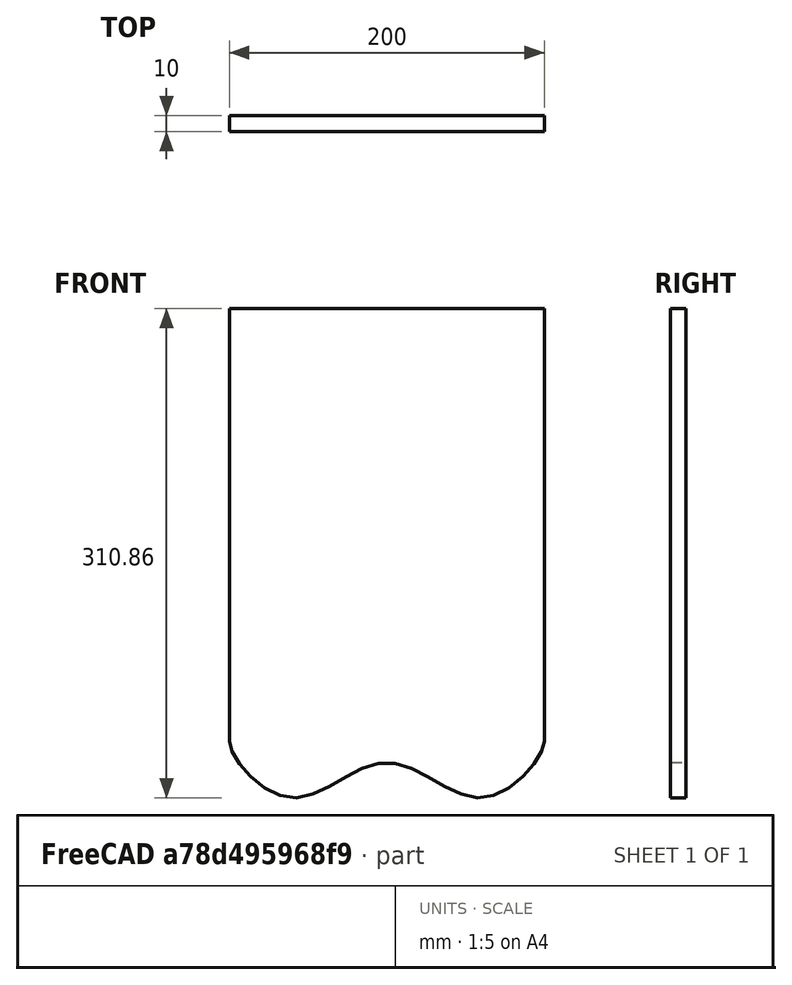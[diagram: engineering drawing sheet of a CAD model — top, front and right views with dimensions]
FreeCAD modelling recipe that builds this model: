
FCSTD DOCUMENT  (FreeCAD 0.17R11311 (Git))
Label: Dach
License: All rights reserved
LicenseURL: http://en.wikipedia.org/wiki/All_rights_reserved
objects: Sketcher::SketchObject×1, PartDesign::Pad×1, PartDesign::Body×1
note: 4 computed .brp shape members not serialized (recipe doc carries the construction recipe); baked Part::Feature solids carry a one-line shape summary decoded from their .brp

FEATURE [Sketcher::SketchObject] Sketch
  MapMode = 5
  Placement = pos=(0,0,0) rot=(1,0,0;1.5708rad)
  Support = -> [XZ_Plane]
  sketch-geometry (29):
    g0: LineSegment StartX=-100 StartY=137.5 StartZ=0 EndX=100 EndY=137.5 EndZ=0
    g1: LineSegment StartX=100 StartY=137.5 StartZ=0 EndX=100 EndY=-137.5 EndZ=0
    g2: LineSegment [constr] StartX=100 StartY=-137.5 StartZ=0 EndX=-100 EndY=-137.5 EndZ=0
    g3: LineSegment StartX=-100 StartY=-137.5 StartZ=0 EndX=-100 EndY=137.5 EndZ=0
    g4: GeomPoint X=0 Y=-127.5 Z=0
    g5: GeomPoint X=0 Y=-137.5 Z=0
    g6: GeomPoint X=-60 Y=-137.5 Z=0
    g7: GeomPoint X=60 Y=-137.5 Z=0
    g8: LineSegment [constr] StartX=-100 StartY=-137.5 StartZ=0 EndX=-100 EndY=-176.893 EndZ=0
    g9: LineSegment [constr] StartX=100 StartY=-137.5 StartZ=0 EndX=100 EndY=-177.603 EndZ=0
    g10: GeomPoint X=-100 Y=-147.5 Z=0
    g11: GeomPoint X=100 Y=-147.5 Z=0
    g12: LineSegment [constr] StartX=-60 StartY=-137.5 StartZ=0 EndX=-60 EndY=-185.392 EndZ=0
    g13: LineSegment [constr] StartX=60 StartY=-137.5 StartZ=0 EndX=60 EndY=-178.519 EndZ=0
    g14: GeomPoint X=-60 Y=-197.5 Z=0
    g15: GeomPoint X=60 Y=-197.5 Z=0
    g16-g22: Circle [constr] x7 (B-spline internal-alignment scaffolding for g23; pole/knot coordinates omitted)
    g23: BSplineCurve PolesCount=7 KnotsCount=5 Degree=3 IsPeriodic=0
    g24-g28: GeomPoint [constr] x5 (B-spline internal-alignment scaffolding for g23; pole/knot coordinates omitted)
  constraints (47):
    c: Coincident(g0,g1)
    c: Coincident(g1,g2)
    c: Coincident(g2,g3)
    c: Coincident(g3,g0)
    c: Horizontal(g0)
    c: Horizontal(g2)
    c: Vertical(g1)
    c: Vertical(g3)
    c: Symmetric(g0,g0,g-2)
    c: Symmetric(g2,g0,g-1)
    c: DistanceY(g1,g1) = 275
    c: DistanceX(g0,g0) = 200
    c: PointOnObject(g4,g-2)
    c: PointOnObject(g5,g-2)
    c: PointOnObject(g5,g2)
    c: DistanceY(g5,g4) = 10
    c: PointOnObject(g6,g2)
    c: PointOnObject(g7,g2)
    c: DistanceX(g2,g6) = 40
    c: DistanceX(g7,g1) = 40
    c: Vertical(g8)
    c: Coincident(g8,g2)
    c: Vertical(g9)
    c: Coincident(g9,g1)
    c: PointOnObject(g10,g8)
    c: PointOnObject(g11,g9)
    c: DistanceY(g10,g2) = 10
    c: DistanceY(g11,g1) = 10
    c: Vertical(g12)
    c: Vertical(g13)
    c: Coincident(g12,g6)
    c: Coincident(g13,g7)
    c: PointOnObject(g14,g12)
    c: PointOnObject(g15,g13)
    c: DistanceY(g14,g6) = 60
    c: DistanceY(g15,g7) = 60
    c: Radius(g16) = 2
    c: Equal(g16, g17-g22) x6
    c: InternalAlignment(g16-g22 -> g23) x7
    c: InternalAlignment(g24-g28 -> g23) x5
    c: Coincident(g16,g2)
    c: Coincident(g17,g10)
    c: Coincident(g18,g14)
    c: Coincident(g19,g4)
    c: Coincident(g22,g1)
    c: Coincident(g21,g11)
    c: Coincident(g20,g15)
FEATURE [PartDesign::Pad] Pad
  Length = 5
  Length2 = 100
  Placement = pos=(0,0,0) rot=(1,0,0;1.5708rad)
  Profile = -> Sketch
  Type = 0
FEATURE [PartDesign::Body] Body
  Group = -> [Sketch,Pad]
  Origin = -> BodyOrigin
  Tip = -> Pad
